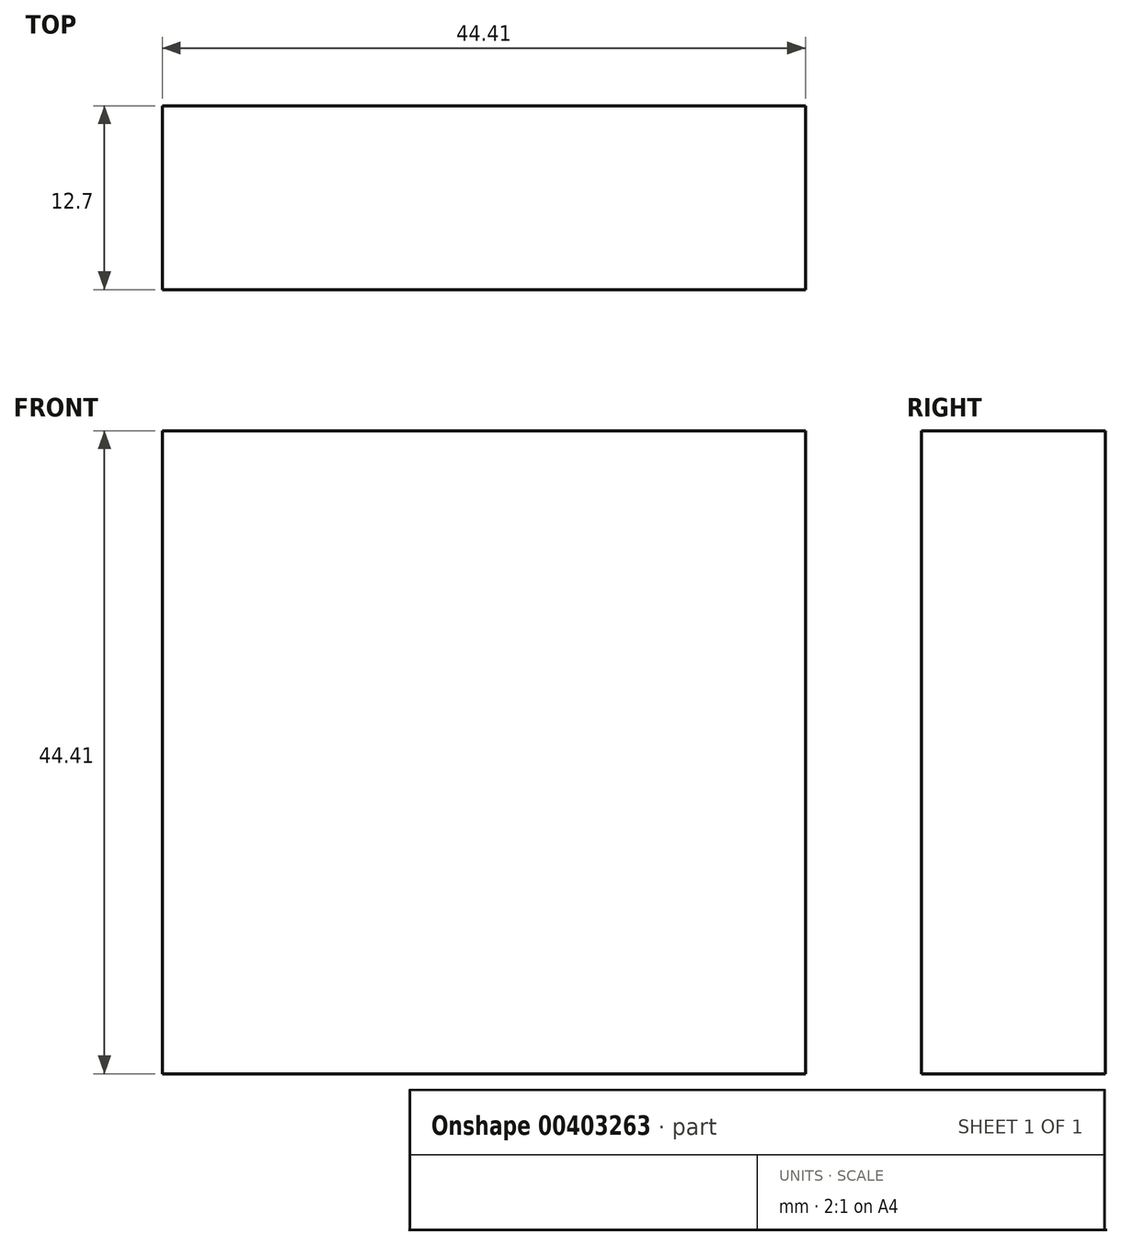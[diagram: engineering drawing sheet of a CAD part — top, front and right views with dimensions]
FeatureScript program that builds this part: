
annotation { "Feature Type Name" : "Feature", "Feature Type Description" : "" }
export const myFeature = defineFeature(function(context is Context, id is Id, definition is map)
    precondition{}
    {
        {
            var Q0;
            Q0=qCreatedBy(makeId("Front.planeOp"),FACE);
            var sketch = newSketch(context, id + "F0", { "sketchPlane" : qUnion([Q0])});
            skLineSegment(sketch, "E0.bottom", {"start": v(0, 0) * mm, "end": v(44.4, 0) * mm});
            skLineSegment(sketch, "E0.top", {"start": v(0, -44.4) * mm, "end": v(44.4, -44.4) * mm});
            skLineSegment(sketch, "E0.left", {"start": v(0, 0) * mm, "end": v(0, -44.4) * mm});
            skLineSegment(sketch, "E0.right", {"start": v(44.4, 0) * mm, "end": v(44.4, -44.4) * mm});
            skLineSegment(sketch, "E1", {"start": v(44.4, -22.2) * mm, "end": v(0, -22.2) * mm, "construction": true});
            skLineSegment(sketch, "E2", {"start": v(22.2, -44.4) * mm, "end": v(22.2, 0) * mm, "construction": true});
            skSolve(sketch);
        }
        {
            var Q0;
            Q0=makeQuery(id+"F0.imprint","IMPRINT",FACE,{"disambiguationData":[TD([[makeQuery(id+"F0.imprint","IMPRINT",EDGE,{"derivedFrom":sQuery(id+"F0.wireOp",EDGE,"E0.bottom")}),-1.0]])]});
            extrude(context, id + "F1", {"entities" : qUnion([Q0]), "depth" : 12.7 * mm});
        }
    });
